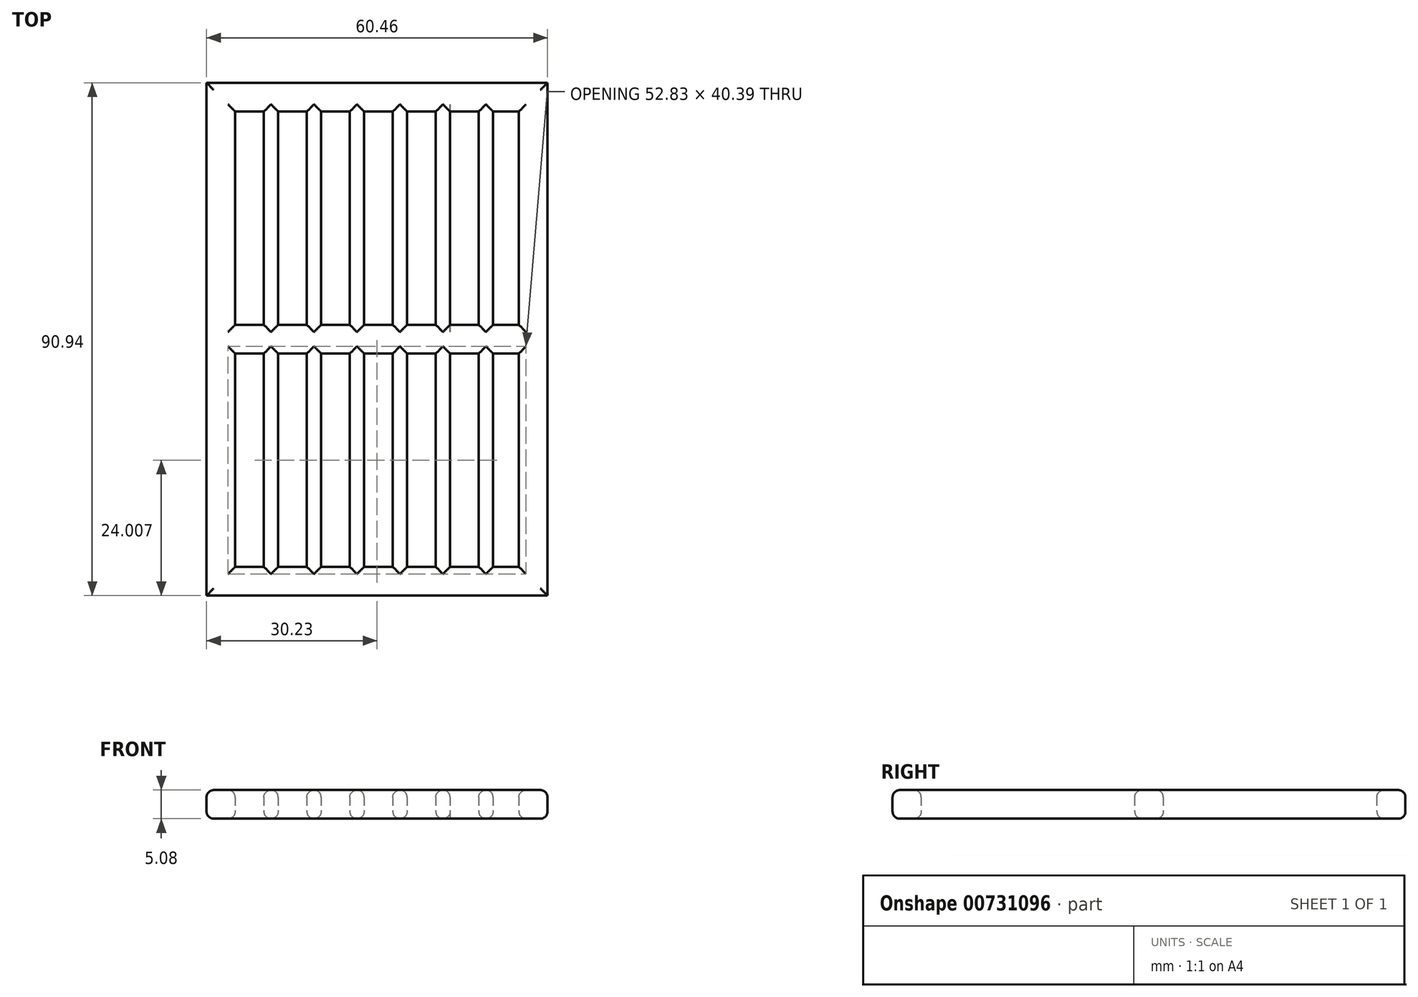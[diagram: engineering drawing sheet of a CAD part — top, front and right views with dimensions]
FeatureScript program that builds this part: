
annotation { "Feature Type Name" : "Feature", "Feature Type Description" : "" }
export const myFeature = defineFeature(function(context is Context, id is Id, definition is map)
    precondition{}
    {
        {
            var Q0;
            Q0=qCreatedBy(makeId("Top.planeOp"),FACE);
            var sketch = newSketch(context, id + "F0", { "sketchPlane" : qUnion([Q0])});
            skLineSegment(sketch, "E0.bottom", {"start": v(-30.23, -45.47) * mm, "end": v(30.23, -45.47) * mm});
            skLineSegment(sketch, "E0.top", {"start": v(-30.23, 45.47) * mm, "end": v(30.23, 45.47) * mm});
            skLineSegment(sketch, "E0.left", {"start": v(-30.23, -45.47) * mm, "end": v(-30.23, 45.47) * mm});
            skLineSegment(sketch, "E0.right", {"start": v(30.23, -45.47) * mm, "end": v(30.23, 45.47) * mm});
            skLineSegment(sketch, "E1.bottom", {"start": v(-25.15, -40.39) * mm, "end": v(25.15, -40.39) * mm});
            skLineSegment(sketch, "E1.top", {"start": v(-25.15, 40.39) * mm, "end": v(25.15, 40.39) * mm});
            skLineSegment(sketch, "E1.left", {"start": v(-25.15, -40.39) * mm, "end": v(-25.15, 40.39) * mm});
            skLineSegment(sketch, "E1.right", {"start": v(25.15, -40.39) * mm, "end": v(25.15, 40.39) * mm});
            skLineSegment(sketch, "E2.bottom", {"start": v(-25.15, 2.54) * mm, "end": v(-2.29, 2.54) * mm});
            skLineSegment(sketch, "E2.top", {"start": v(-25.15, -2.54) * mm, "end": v(25.15, -2.54) * mm});
            skLineSegment(sketch, "E2.left", {"start": v(-25.15, 2.54) * mm, "end": v(-25.15, -2.54) * mm});
            skLineSegment(sketch, "E2.right", {"start": v(25.15, 2.54) * mm, "end": v(25.15, -2.54) * mm});
            skLineSegment(sketch, "E3.bottom", {"start": v(-20.07, 2.54) * mm, "end": v(-17.53, 2.54) * mm});
            skLineSegment(sketch, "E3.top", {"start": v(-20.07, 40.39) * mm, "end": v(-17.53, 40.39) * mm});
            skLineSegment(sketch, "E3.left", {"start": v(-20.07, 2.54) * mm, "end": v(-20.07, 40.39) * mm});
            skLineSegment(sketch, "E3.right", {"start": v(-17.53, 2.54) * mm, "end": v(-17.53, 40.39) * mm});
            skLineSegment(sketch, "E4.bottom", {"start": v(-12.45, 2.54) * mm, "end": v(-9.9, 2.54) * mm});
            skLineSegment(sketch, "E4.top", {"start": v(-12.45, 40.39) * mm, "end": v(-9.9, 40.39) * mm});
            skLineSegment(sketch, "E4.left", {"start": v(-12.45, 2.54) * mm, "end": v(-12.45, 40.39) * mm});
            skLineSegment(sketch, "E4.right", {"start": v(-9.9, 2.54) * mm, "end": v(-9.9, 40.39) * mm});
            skLineSegment(sketch, "E5.bottom", {"start": v(-4.83, 2.54) * mm, "end": v(-2.29, 2.54) * mm});
            skLineSegment(sketch, "E5.top", {"start": v(-4.83, 40.39) * mm, "end": v(-2.29, 40.39) * mm});
            skLineSegment(sketch, "E5.left", {"start": v(-4.83, 2.54) * mm, "end": v(-4.83, 40.39) * mm});
            skLineSegment(sketch, "E5.right", {"start": v(-2.29, 2.54) * mm, "end": v(-2.29, 40.39) * mm});
            skLineSegment(sketch, "E6.bottom", {"start": v(10.41, 2.54) * mm, "end": v(12.95, 2.54) * mm});
            skLineSegment(sketch, "E6.top", {"start": v(10.41, 40.39) * mm, "end": v(12.95, 40.39) * mm});
            skLineSegment(sketch, "E6.left", {"start": v(10.41, 2.54) * mm, "end": v(10.41, 40.39) * mm});
            skLineSegment(sketch, "E6.right", {"start": v(12.95, 2.54) * mm, "end": v(12.95, 40.39) * mm});
            skLineSegment(sketch, "E7.bottom", {"start": v(18.03, 2.54) * mm, "end": v(20.57, 2.54) * mm});
            skLineSegment(sketch, "E7.top", {"start": v(18.03, 40.39) * mm, "end": v(20.57, 40.39) * mm});
            skLineSegment(sketch, "E7.left", {"start": v(18.03, 2.54) * mm, "end": v(18.03, 40.39) * mm});
            skLineSegment(sketch, "E7.right", {"start": v(20.57, 2.54) * mm, "end": v(20.57, 40.39) * mm});
            skLineSegment(sketch, "E8.trimOffspring", {"start": v(10.41, 2.54) * mm, "end": v(25.15, 2.54) * mm});
            skLineSegment(sketch, "E9.bottom", {"start": v(5.33, 2.54) * mm, "end": v(2.8, 2.54) * mm});
            skLineSegment(sketch, "E9.top", {"start": v(5.33, 40.39) * mm, "end": v(2.8, 40.39) * mm});
            skLineSegment(sketch, "E9.left", {"start": v(5.33, 2.54) * mm, "end": v(5.33, 40.39) * mm});
            skLineSegment(sketch, "E9.right", {"start": v(2.8, 2.54) * mm, "end": v(2.8, 40.39) * mm});
            skLineSegment(sketch, "E10.MirrorCS", {"start": v(-20.07, -2.54) * mm, "end": v(-20.07, -40.39) * mm});
            skLineSegment(sketch, "E11.MirrorCS", {"start": v(-17.53, -2.54) * mm, "end": v(-17.53, -40.39) * mm});
            skLineSegment(sketch, "E12.MirrorCS", {"start": v(-12.45, -2.54) * mm, "end": v(-12.45, -40.39) * mm});
            skLineSegment(sketch, "E13.MirrorCS", {"start": v(-9.9, -2.54) * mm, "end": v(-9.9, -40.39) * mm});
            skLineSegment(sketch, "E14.MirrorCS", {"start": v(-4.83, -2.54) * mm, "end": v(-4.83, -40.39) * mm});
            skLineSegment(sketch, "E15.MirrorCS", {"start": v(-2.29, -2.54) * mm, "end": v(-2.29, -40.39) * mm});
            skLineSegment(sketch, "E16.MirrorCS", {"start": v(2.8, -2.54) * mm, "end": v(2.8, -40.39) * mm});
            skLineSegment(sketch, "E17.MirrorCS", {"start": v(5.33, -2.54) * mm, "end": v(5.33, -40.39) * mm});
            skLineSegment(sketch, "E18.MirrorCS", {"start": v(10.41, -2.54) * mm, "end": v(10.41, -40.39) * mm});
            skLineSegment(sketch, "E19.MirrorCS", {"start": v(12.95, -2.54) * mm, "end": v(12.95, -40.39) * mm});
            skLineSegment(sketch, "E20.MirrorCS", {"start": v(18.03, -2.54) * mm, "end": v(18.03, -40.39) * mm});
            skLineSegment(sketch, "E21.MirrorCS", {"start": v(20.57, -2.54) * mm, "end": v(20.57, -40.39) * mm});
            skLineSegment(sketch, "E22", {"start": v(-2.29, 2.54) * mm, "end": v(2.8, 2.54) * mm});
            skLineSegment(sketch, "E23", {"start": v(5.33, 2.54) * mm, "end": v(10.41, 2.54) * mm});
            skSolve(sketch);
        }
        {
            var Q0;
            Q0=makeQuery(id+"F0.imprint","IMPRINT",FACE,{"disambiguationData":[TD([[makeQuery(id+"F0.imprint","IMPRINT",EDGE,{"derivedFrom":sQuery(id+"F0.wireOp",EDGE,"E0.bottom")}),1.0]])]});
            var Q1;
            {var subQ25=sQuery(id+"F0.wireOp",EDGE,"E6.bottom");Q1=makeQuery(id+"F0.imprint","IMPRINT",FACE,{"disambiguationData":[TD([[makeQuery(id+"F0.imprint","IMPRINT",EDGE,{"derivedFrom":subQ25}),-1.0]])]});}
            var Q2;
            {var subQ0=sQuery(id+"F0.wireOp",EDGE,"E10.MirrorCS");Q2=makeQuery(id+"F0.imprint","IMPRINT",FACE,{"disambiguationData":[TD([[makeQuery(id+"F0.imprint","IMPRINT",EDGE,{"derivedFrom":subQ0}),1.0]])]});}
            var Q3;
            {var subQ2=sQuery(id+"F0.wireOp",EDGE,"E12.MirrorCS");Q3=makeQuery(id+"F0.imprint","IMPRINT",FACE,{"disambiguationData":[TD([[makeQuery(id+"F0.imprint","IMPRINT",EDGE,{"derivedFrom":subQ2}),1.0]])]});}
            var Q4;
            {var subQ0=sQuery(id+"F0.wireOp",EDGE,"E14.MirrorCS");Q4=makeQuery(id+"F0.imprint","IMPRINT",FACE,{"disambiguationData":[TD([[makeQuery(id+"F0.imprint","IMPRINT",EDGE,{"derivedFrom":subQ0}),1.0]])]});}
            var Q5;
            {var subQ0=sQuery(id+"F0.wireOp",EDGE,"E16.MirrorCS");Q5=makeQuery(id+"F0.imprint","IMPRINT",FACE,{"disambiguationData":[TD([[makeQuery(id+"F0.imprint","IMPRINT",EDGE,{"derivedFrom":subQ0}),1.0]])]});}
            var Q6;
            {var subQ0=sQuery(id+"F0.wireOp",EDGE,"E18.MirrorCS");Q6=makeQuery(id+"F0.imprint","IMPRINT",FACE,{"disambiguationData":[TD([[makeQuery(id+"F0.imprint","IMPRINT",EDGE,{"derivedFrom":subQ0}),1.0]])]});}
            var Q7;
            {var subQ0=sQuery(id+"F0.wireOp",EDGE,"E20.MirrorCS");Q7=makeQuery(id+"F0.imprint","IMPRINT",FACE,{"disambiguationData":[TD([[makeQuery(id+"F0.imprint","IMPRINT",EDGE,{"derivedFrom":subQ0}),1.0]])]});}
            var Q8;
            Q8=makeQuery(id+"F0.imprint","IMPRINT",FACE,{"disambiguationData":[TD([[makeQuery(id+"F0.imprint","IMPRINT",EDGE,{"derivedFrom":sQuery(id+"F0.wireOp",EDGE,"E7.bottom")}),1.0]])]});
            var Q9;
            Q9=makeQuery(id+"F0.imprint","IMPRINT",FACE,{"disambiguationData":[TD([[makeQuery(id+"F0.imprint","IMPRINT",EDGE,{"derivedFrom":sQuery(id+"F0.wireOp",EDGE,"E6.bottom")}),1.0]])]});
            var Q10;
            Q10=makeQuery(id+"F0.imprint","IMPRINT",FACE,{"disambiguationData":[TD([[makeQuery(id+"F0.imprint","IMPRINT",EDGE,{"derivedFrom":sQuery(id+"F0.wireOp",EDGE,"E9.bottom")}),-1.0]])]});
            var Q11;
            {var subQ0=sQuery(id+"F0.wireOp",EDGE,"E5.left");Q11=makeQuery(id+"F0.imprint","IMPRINT",FACE,{"disambiguationData":[TD([[makeQuery(id+"F0.imprint","IMPRINT",EDGE,{"derivedFrom":subQ0}),-1.0]])]});}
            var Q12;
            {var subQ0=sQuery(id+"F0.wireOp",EDGE,"E4.left");Q12=makeQuery(id+"F0.imprint","IMPRINT",FACE,{"disambiguationData":[TD([[makeQuery(id+"F0.imprint","IMPRINT",EDGE,{"derivedFrom":subQ0}),-1.0]])]});}
            var Q13;
            {var subQ0=sQuery(id+"F0.wireOp",EDGE,"E3.left");Q13=makeQuery(id+"F0.imprint","IMPRINT",FACE,{"disambiguationData":[TD([[makeQuery(id+"F0.imprint","IMPRINT",EDGE,{"derivedFrom":subQ0}),-1.0]])]});}
            extrude(context, id + "F1", {"entities" : qUnion([Q0, Q1, Q2, Q3, Q4, Q5, Q6, Q7, Q8, Q9, Q10, Q11, Q12, Q13]), "depth" : 5.08 * mm, "offsetDistance" : 25.4 * mm});
        }
        {
            var Q0;
            Q0=makeQuery(id+"F1.opExtrude","CAP_EDGE",EDGE,{"disambiguationData":[OSD([sQuery(id+"F0.wireOp",EDGE,"E3.left")])],"isStart":false});
            var Q1;
            {var subQ0=sQuery(id+"F0.wireOp",EDGE,"E1.top");Q1=makeQuery(id+"F1.opExtrude","CAP_EDGE",EDGE,{"disambiguationData":[OSD([subQ0]),TDD([makeQuery(id+"F0.imprint","IMPRINT",EDGE,{"disambiguationData":[TD([[makeQuery(id+"F0.imprint","INTERSECT",VERTEX,{"derivedFrom":[subQ0,sQuery(id+"F0.wireOp",EDGE,"E3.left")]}),1.0]])],"derivedFrom":subQ0})])],"isStart":false});}
            var Q2;
            {var subQ0=sQuery(id+"F0.wireOp",EDGE,"E1.left");Q2=makeQuery(id+"F1.opExtrude","CAP_EDGE",EDGE,{"disambiguationData":[OSD([subQ0]),TDD([makeQuery(id+"F0.imprint","IMPRINT",EDGE,{"disambiguationData":[TD([[makeQuery(id+"F0.imprint","INTERSECT",VERTEX,{"derivedFrom":[subQ0,sQuery(id+"F0.wireOp",EDGE,"E2.bottom")]}),-1.0]])],"derivedFrom":subQ0})])],"isStart":false});}
            var Q3;
            {var subQ0=sQuery(id+"F0.wireOp",EDGE,"E2.bottom");Q3=makeQuery(id+"F1.opExtrude","CAP_EDGE",EDGE,{"disambiguationData":[OSD([subQ0]),TDD([makeQuery(id+"F0.imprint","IMPRINT",EDGE,{"disambiguationData":[TD([[makeQuery(id+"F0.imprint","INTERSECT",VERTEX,{"derivedFrom":[sQuery(id+"F0.wireOp",EDGE,"E1.left"),subQ0]}),-1.0]])],"derivedFrom":subQ0})])],"isStart":false});}
            var Q4;
            Q4=makeQuery(id+"F1.opExtrude","CAP_EDGE",EDGE,{"disambiguationData":[OSD([sQuery(id+"F0.wireOp",EDGE,"E3.right")])],"isStart":false});
            var Q5;
            Q5=makeQuery(id+"F1.opExtrude","CAP_EDGE",EDGE,{"disambiguationData":[OSD([sQuery(id+"F0.wireOp",EDGE,"E4.left")])],"isStart":false});
            var Q6;
            {var subQ0=sQuery(id+"F0.wireOp",EDGE,"E1.top");Q6=makeQuery(id+"F1.opExtrude","CAP_EDGE",EDGE,{"disambiguationData":[OSD([subQ0]),TDD([makeQuery(id+"F0.imprint","IMPRINT",EDGE,{"disambiguationData":[TD([[makeQuery(id+"F0.imprint","INTERSECT",VERTEX,{"derivedFrom":[subQ0,sQuery(id+"F0.wireOp",EDGE,"E3.right")]}),-1.0]])],"derivedFrom":subQ0})])],"isStart":false});}
            var Q7;
            {var subQ0=sQuery(id+"F0.wireOp",EDGE,"E2.bottom");Q7=makeQuery(id+"F1.opExtrude","CAP_EDGE",EDGE,{"disambiguationData":[OSD([subQ0]),TDD([makeQuery(id+"F0.imprint","IMPRINT",EDGE,{"disambiguationData":[TD([[makeQuery(id+"F0.imprint","INTERSECT",VERTEX,{"derivedFrom":[subQ0,sQuery(id+"F0.wireOp",EDGE,"E3.right")]}),-1.0]])],"derivedFrom":subQ0})])],"isStart":false});}
            var Q8;
            {var subQ0=sQuery(id+"F0.wireOp",EDGE,"E2.bottom");Q8=makeQuery(id+"F1.opExtrude","CAP_EDGE",EDGE,{"disambiguationData":[OSD([subQ0]),TDD([makeQuery(id+"F0.imprint","IMPRINT",EDGE,{"disambiguationData":[TD([[makeQuery(id+"F0.imprint","INTERSECT",VERTEX,{"derivedFrom":[subQ0,sQuery(id+"F0.wireOp",EDGE,"E4.right")]}),-1.0]])],"derivedFrom":subQ0})])],"isStart":false});}
            var Q9;
            Q9=makeQuery(id+"F1.opExtrude","CAP_EDGE",EDGE,{"disambiguationData":[OSD([sQuery(id+"F0.wireOp",EDGE,"E5.left")])],"isStart":false});
            var Q10;
            Q10=makeQuery(id+"F1.opExtrude","CAP_EDGE",EDGE,{"disambiguationData":[OSD([sQuery(id+"F0.wireOp",EDGE,"E4.right")])],"isStart":false});
            var Q11;
            {var subQ0=sQuery(id+"F0.wireOp",EDGE,"E1.top");Q11=makeQuery(id+"F1.opExtrude","CAP_EDGE",EDGE,{"disambiguationData":[OSD([subQ0]),TDD([makeQuery(id+"F0.imprint","IMPRINT",EDGE,{"disambiguationData":[TD([[makeQuery(id+"F0.imprint","INTERSECT",VERTEX,{"derivedFrom":[subQ0,sQuery(id+"F0.wireOp",EDGE,"E4.right")]}),-1.0]])],"derivedFrom":subQ0})])],"isStart":false});}
            var Q12;
            Q12=makeQuery(id+"F1.opExtrude","CAP_EDGE",EDGE,{"disambiguationData":[OSD([sQuery(id+"F0.wireOp",EDGE,"E5.right")])],"isStart":false});
            var Q13;
            Q13=makeQuery(id+"F1.opExtrude","CAP_EDGE",EDGE,{"disambiguationData":[OSD([sQuery(id+"F0.wireOp",EDGE,"E9.right")])],"isStart":false});
            var Q14;
            {var subQ0=sQuery(id+"F0.wireOp",EDGE,"E1.top");Q14=makeQuery(id+"F1.opExtrude","CAP_EDGE",EDGE,{"disambiguationData":[OSD([subQ0]),TDD([makeQuery(id+"F0.imprint","IMPRINT",EDGE,{"disambiguationData":[TD([[makeQuery(id+"F0.imprint","INTERSECT",VERTEX,{"derivedFrom":[subQ0,sQuery(id+"F0.wireOp",EDGE,"E5.right")]}),-1.0]])],"derivedFrom":subQ0})])],"isStart":false});}
            var Q15;
            Q15=makeQuery(id+"F1.opExtrude","CAP_EDGE",EDGE,{"disambiguationData":[OSD([sQuery(id+"F0.wireOp",EDGE,"E22")])],"isStart":false});
            var Q16;
            Q16=makeQuery(id+"F1.opExtrude","CAP_EDGE",EDGE,{"disambiguationData":[OSD([sQuery(id+"F0.wireOp",EDGE,"E9.left")])],"isStart":false});
            var Q17;
            Q17=makeQuery(id+"F1.opExtrude","CAP_EDGE",EDGE,{"disambiguationData":[OSD([sQuery(id+"F0.wireOp",EDGE,"E23")])],"isStart":false});
            var Q18;
            Q18=makeQuery(id+"F1.opExtrude","CAP_EDGE",EDGE,{"disambiguationData":[OSD([sQuery(id+"F0.wireOp",EDGE,"E6.left")])],"isStart":false});
            var Q19;
            {var subQ0=sQuery(id+"F0.wireOp",EDGE,"E1.top");Q19=makeQuery(id+"F1.opExtrude","CAP_EDGE",EDGE,{"disambiguationData":[OSD([subQ0]),TDD([makeQuery(id+"F0.imprint","IMPRINT",EDGE,{"disambiguationData":[TD([[makeQuery(id+"F0.imprint","INTERSECT",VERTEX,{"derivedFrom":[subQ0,sQuery(id+"F0.wireOp",EDGE,"E9.left")]}),-1.0]])],"derivedFrom":subQ0})])],"isStart":false});}
            var Q20;
            Q20=makeQuery(id+"F1.opExtrude","CAP_EDGE",EDGE,{"disambiguationData":[OSD([sQuery(id+"F0.wireOp",EDGE,"E6.right")])],"isStart":false});
            var Q21;
            Q21=makeQuery(id+"F1.opExtrude","CAP_EDGE",EDGE,{"disambiguationData":[OSD([sQuery(id+"F0.wireOp",EDGE,"E7.left")])],"isStart":false});
            var Q22;
            {var subQ0=sQuery(id+"F0.wireOp",EDGE,"E8.trimOffspring");Q22=makeQuery(id+"F1.opExtrude","CAP_EDGE",EDGE,{"disambiguationData":[OSD([subQ0]),TDD([makeQuery(id+"F0.imprint","IMPRINT",EDGE,{"disambiguationData":[TD([[makeQuery(id+"F0.imprint","INTERSECT",VERTEX,{"derivedFrom":[sQuery(id+"F0.wireOp",EDGE,"E6.bottom"),sQuery(id+"F0.wireOp",EDGE,"E6.right"),subQ0]}),-1.0]])],"derivedFrom":subQ0})])],"isStart":false});}
            var Q23;
            {var subQ0=sQuery(id+"F0.wireOp",EDGE,"E1.top");Q23=makeQuery(id+"F1.opExtrude","CAP_EDGE",EDGE,{"disambiguationData":[OSD([subQ0]),TDD([makeQuery(id+"F0.imprint","IMPRINT",EDGE,{"disambiguationData":[TD([[makeQuery(id+"F0.imprint","INTERSECT",VERTEX,{"derivedFrom":[subQ0,sQuery(id+"F0.wireOp",EDGE,"E6.right")]}),-1.0]])],"derivedFrom":subQ0})])],"isStart":false});}
            var Q24;
            {var subQ0=sQuery(id+"F0.wireOp",EDGE,"E1.top");Q24=makeQuery(id+"F1.opExtrude","CAP_EDGE",EDGE,{"disambiguationData":[OSD([subQ0]),TDD([makeQuery(id+"F0.imprint","IMPRINT",EDGE,{"disambiguationData":[TD([[makeQuery(id+"F0.imprint","INTERSECT",VERTEX,{"derivedFrom":[subQ0,sQuery(id+"F0.wireOp",EDGE,"E7.right")]}),-1.0]])],"derivedFrom":subQ0})])],"isStart":false});}
            var Q25;
            {var subQ0=sQuery(id+"F0.wireOp",EDGE,"E1.right");Q25=makeQuery(id+"F1.opExtrude","CAP_EDGE",EDGE,{"disambiguationData":[OSD([subQ0]),TDD([makeQuery(id+"F0.imprint","IMPRINT",EDGE,{"disambiguationData":[TD([[makeQuery(id+"F0.imprint","INTERSECT",VERTEX,{"derivedFrom":[subQ0,sQuery(id+"F0.wireOp",EDGE,"E8.trimOffspring")]}),-1.0]])],"derivedFrom":subQ0})])],"isStart":false});}
            var Q26;
            Q26=makeQuery(id+"F1.opExtrude","CAP_EDGE",EDGE,{"disambiguationData":[OSD([sQuery(id+"F0.wireOp",EDGE,"E7.right")])],"isStart":false});
            var Q27;
            {var subQ0=sQuery(id+"F0.wireOp",EDGE,"E8.trimOffspring");Q27=makeQuery(id+"F1.opExtrude","CAP_EDGE",EDGE,{"disambiguationData":[OSD([subQ0]),TDD([makeQuery(id+"F0.imprint","IMPRINT",EDGE,{"disambiguationData":[TD([[makeQuery(id+"F0.imprint","INTERSECT",VERTEX,{"derivedFrom":[sQuery(id+"F0.wireOp",EDGE,"E1.right"),subQ0]}),1.0]])],"derivedFrom":subQ0})])],"isStart":false});}
            var Q28;
            {var subQ0=sQuery(id+"F0.wireOp",EDGE,"E1.right");Q28=makeQuery(id+"F1.opExtrude","CAP_EDGE",EDGE,{"disambiguationData":[OSD([subQ0]),TDD([makeQuery(id+"F0.imprint","IMPRINT",EDGE,{"disambiguationData":[TD([[makeQuery(id+"F0.imprint","INTERSECT",VERTEX,{"derivedFrom":[sQuery(id+"F0.wireOp",EDGE,"E1.bottom"),subQ0]}),-1.0]])],"derivedFrom":subQ0})])],"isStart":false});}
            var Q29;
            Q29=makeQuery(id+"F1.opExtrude","CAP_EDGE",EDGE,{"disambiguationData":[OSD([sQuery(id+"F0.wireOp",EDGE,"E21.MirrorCS")])],"isStart":false});
            var Q30;
            {var subQ0=sQuery(id+"F0.wireOp",EDGE,"E2.top");Q30=makeQuery(id+"F1.opExtrude","CAP_EDGE",EDGE,{"disambiguationData":[OSD([subQ0]),TDD([makeQuery(id+"F0.imprint","IMPRINT",EDGE,{"disambiguationData":[TD([[makeQuery(id+"F0.imprint","INTERSECT",VERTEX,{"derivedFrom":[subQ0,sQuery(id+"F0.wireOp",EDGE,"E21.MirrorCS")]}),-1.0]])],"derivedFrom":subQ0})])],"isStart":false});}
            var Q31;
            {var subQ0=sQuery(id+"F0.wireOp",EDGE,"E1.bottom");Q31=makeQuery(id+"F1.opExtrude","CAP_EDGE",EDGE,{"disambiguationData":[OSD([subQ0]),TDD([makeQuery(id+"F0.imprint","IMPRINT",EDGE,{"disambiguationData":[TD([[makeQuery(id+"F0.imprint","INTERSECT",VERTEX,{"derivedFrom":[subQ0,sQuery(id+"F0.wireOp",EDGE,"E1.right")]}),1.0]])],"derivedFrom":subQ0})])],"isStart":false});}
            var Q32;
            {var subQ0=sQuery(id+"F0.wireOp",EDGE,"E1.bottom");Q32=makeQuery(id+"F1.opExtrude","CAP_EDGE",EDGE,{"disambiguationData":[OSD([subQ0]),TDD([makeQuery(id+"F0.imprint","IMPRINT",EDGE,{"disambiguationData":[TD([[makeQuery(id+"F0.imprint","INTERSECT",VERTEX,{"derivedFrom":[subQ0,sQuery(id+"F0.wireOp",EDGE,"E19.MirrorCS")]}),-1.0]])],"derivedFrom":subQ0})])],"isStart":false});}
            var Q33;
            Q33=makeQuery(id+"F1.opExtrude","CAP_EDGE",EDGE,{"disambiguationData":[OSD([sQuery(id+"F0.wireOp",EDGE,"E20.MirrorCS")])],"isStart":false});
            var Q34;
            Q34=makeQuery(id+"F1.opExtrude","CAP_EDGE",EDGE,{"disambiguationData":[OSD([sQuery(id+"F0.wireOp",EDGE,"E19.MirrorCS")])],"isStart":false});
            var Q35;
            {var subQ0=sQuery(id+"F0.wireOp",EDGE,"E2.top");Q35=makeQuery(id+"F1.opExtrude","CAP_EDGE",EDGE,{"disambiguationData":[OSD([subQ0]),TDD([makeQuery(id+"F0.imprint","IMPRINT",EDGE,{"disambiguationData":[TD([[makeQuery(id+"F0.imprint","INTERSECT",VERTEX,{"derivedFrom":[subQ0,sQuery(id+"F0.wireOp",EDGE,"E19.MirrorCS")]}),-1.0]])],"derivedFrom":subQ0})])],"isStart":false});}
            var Q36;
            {var subQ0=sQuery(id+"F0.wireOp",EDGE,"E2.top");Q36=makeQuery(id+"F1.opExtrude","CAP_EDGE",EDGE,{"disambiguationData":[OSD([subQ0]),TDD([makeQuery(id+"F0.imprint","IMPRINT",EDGE,{"disambiguationData":[TD([[makeQuery(id+"F0.imprint","INTERSECT",VERTEX,{"derivedFrom":[subQ0,sQuery(id+"F0.wireOp",EDGE,"E17.MirrorCS")]}),-1.0]])],"derivedFrom":subQ0})])],"isStart":false});}
            var Q37;
            Q37=makeQuery(id+"F1.opExtrude","CAP_EDGE",EDGE,{"disambiguationData":[OSD([sQuery(id+"F0.wireOp",EDGE,"E17.MirrorCS")])],"isStart":false});
            var Q38;
            Q38=makeQuery(id+"F1.opExtrude","CAP_EDGE",EDGE,{"disambiguationData":[OSD([sQuery(id+"F0.wireOp",EDGE,"E18.MirrorCS")])],"isStart":false});
            var Q39;
            {var subQ0=sQuery(id+"F0.wireOp",EDGE,"E1.bottom");Q39=makeQuery(id+"F1.opExtrude","CAP_EDGE",EDGE,{"disambiguationData":[OSD([subQ0]),TDD([makeQuery(id+"F0.imprint","IMPRINT",EDGE,{"disambiguationData":[TD([[makeQuery(id+"F0.imprint","INTERSECT",VERTEX,{"derivedFrom":[subQ0,sQuery(id+"F0.wireOp",EDGE,"E17.MirrorCS")]}),-1.0]])],"derivedFrom":subQ0})])],"isStart":false});}
            var Q40;
            Q40=makeQuery(id+"F1.opExtrude","CAP_EDGE",EDGE,{"disambiguationData":[OSD([sQuery(id+"F0.wireOp",EDGE,"E15.MirrorCS")])],"isStart":false});
            var Q41;
            Q41=makeQuery(id+"F1.opExtrude","CAP_EDGE",EDGE,{"disambiguationData":[OSD([sQuery(id+"F0.wireOp",EDGE,"E16.MirrorCS")])],"isStart":false});
            var Q42;
            {var subQ0=sQuery(id+"F0.wireOp",EDGE,"E1.bottom");Q42=makeQuery(id+"F1.opExtrude","CAP_EDGE",EDGE,{"disambiguationData":[OSD([subQ0]),TDD([makeQuery(id+"F0.imprint","IMPRINT",EDGE,{"disambiguationData":[TD([[makeQuery(id+"F0.imprint","INTERSECT",VERTEX,{"derivedFrom":[subQ0,sQuery(id+"F0.wireOp",EDGE,"E15.MirrorCS")]}),-1.0]])],"derivedFrom":subQ0})])],"isStart":false});}
            var Q43;
            {var subQ0=sQuery(id+"F0.wireOp",EDGE,"E2.top");Q43=makeQuery(id+"F1.opExtrude","CAP_EDGE",EDGE,{"disambiguationData":[OSD([subQ0]),TDD([makeQuery(id+"F0.imprint","IMPRINT",EDGE,{"disambiguationData":[TD([[makeQuery(id+"F0.imprint","INTERSECT",VERTEX,{"derivedFrom":[subQ0,sQuery(id+"F0.wireOp",EDGE,"E15.MirrorCS")]}),-1.0]])],"derivedFrom":subQ0})])],"isStart":false});}
            var Q44;
            Q44=makeQuery(id+"F1.opExtrude","CAP_EDGE",EDGE,{"disambiguationData":[OSD([sQuery(id+"F0.wireOp",EDGE,"E14.MirrorCS")])],"isStart":false});
            var Q45;
            Q45=makeQuery(id+"F1.opExtrude","CAP_EDGE",EDGE,{"disambiguationData":[OSD([sQuery(id+"F0.wireOp",EDGE,"E13.MirrorCS")])],"isStart":false});
            var Q46;
            {var subQ0=sQuery(id+"F0.wireOp",EDGE,"E2.top");Q46=makeQuery(id+"F1.opExtrude","CAP_EDGE",EDGE,{"disambiguationData":[OSD([subQ0]),TDD([makeQuery(id+"F0.imprint","IMPRINT",EDGE,{"disambiguationData":[TD([[makeQuery(id+"F0.imprint","INTERSECT",VERTEX,{"derivedFrom":[subQ0,sQuery(id+"F0.wireOp",EDGE,"E13.MirrorCS")]}),-1.0]])],"derivedFrom":subQ0})])],"isStart":false});}
            var Q47;
            {var subQ0=sQuery(id+"F0.wireOp",EDGE,"E1.bottom");Q47=makeQuery(id+"F1.opExtrude","CAP_EDGE",EDGE,{"disambiguationData":[OSD([subQ0]),TDD([makeQuery(id+"F0.imprint","IMPRINT",EDGE,{"disambiguationData":[TD([[makeQuery(id+"F0.imprint","INTERSECT",VERTEX,{"derivedFrom":[subQ0,sQuery(id+"F0.wireOp",EDGE,"E13.MirrorCS")]}),-1.0]])],"derivedFrom":subQ0})])],"isStart":false});}
            var Q48;
            {var subQ0=sQuery(id+"F0.wireOp",EDGE,"E1.bottom");Q48=makeQuery(id+"F1.opExtrude","CAP_EDGE",EDGE,{"disambiguationData":[OSD([subQ0]),TDD([makeQuery(id+"F0.imprint","IMPRINT",EDGE,{"disambiguationData":[TD([[makeQuery(id+"F0.imprint","INTERSECT",VERTEX,{"derivedFrom":[subQ0,sQuery(id+"F0.wireOp",EDGE,"E11.MirrorCS")]}),-1.0]])],"derivedFrom":subQ0})])],"isStart":false});}
            var Q49;
            {var subQ0=sQuery(id+"F0.wireOp",EDGE,"E2.top");Q49=makeQuery(id+"F1.opExtrude","CAP_EDGE",EDGE,{"disambiguationData":[OSD([subQ0]),TDD([makeQuery(id+"F0.imprint","IMPRINT",EDGE,{"disambiguationData":[TD([[makeQuery(id+"F0.imprint","INTERSECT",VERTEX,{"derivedFrom":[subQ0,sQuery(id+"F0.wireOp",EDGE,"E11.MirrorCS")]}),-1.0]])],"derivedFrom":subQ0})])],"isStart":false});}
            var Q50;
            Q50=makeQuery(id+"F1.opExtrude","CAP_EDGE",EDGE,{"disambiguationData":[OSD([sQuery(id+"F0.wireOp",EDGE,"E11.MirrorCS")])],"isStart":false});
            var Q51;
            Q51=makeQuery(id+"F1.opExtrude","CAP_EDGE",EDGE,{"disambiguationData":[OSD([sQuery(id+"F0.wireOp",EDGE,"E12.MirrorCS")])],"isStart":false});
            var Q52;
            Q52=makeQuery(id+"F1.opExtrude","CAP_FACE",FACE,{"disambiguationData":[OSD([sQuery(id+"F0.wireOp",EDGE,"E0.bottom"),sQuery(id+"F0.wireOp",EDGE,"E0.top"),sQuery(id+"F0.wireOp",EDGE,"E0.left"),sQuery(id+"F0.wireOp",EDGE,"E0.right"),sQuery(id+"F0.wireOp",EDGE,"E1.bottom"),sQuery(id+"F0.wireOp",EDGE,"E1.top"),sQuery(id+"F0.wireOp",EDGE,"E1.left"),sQuery(id+"F0.wireOp",EDGE,"E1.right"),sQuery(id+"F0.wireOp",EDGE,"E2.bottom"),sQuery(id+"F0.wireOp",EDGE,"E2.top"),sQuery(id+"F0.wireOp",EDGE,"E3.left"),sQuery(id+"F0.wireOp",EDGE,"E3.right"),sQuery(id+"F0.wireOp",EDGE,"E4.left"),sQuery(id+"F0.wireOp",EDGE,"E4.right"),sQuery(id+"F0.wireOp",EDGE,"E5.left"),sQuery(id+"F0.wireOp",EDGE,"E5.right"),sQuery(id+"F0.wireOp",EDGE,"E6.left"),sQuery(id+"F0.wireOp",EDGE,"E6.right"),sQuery(id+"F0.wireOp",EDGE,"E7.left"),sQuery(id+"F0.wireOp",EDGE,"E7.right"),sQuery(id+"F0.wireOp",EDGE,"E8.trimOffspring"),sQuery(id+"F0.wireOp",EDGE,"E9.left"),sQuery(id+"F0.wireOp",EDGE,"E9.right"),sQuery(id+"F0.wireOp",EDGE,"E10.MirrorCS"),sQuery(id+"F0.wireOp",EDGE,"E11.MirrorCS"),sQuery(id+"F0.wireOp",EDGE,"E12.MirrorCS"),sQuery(id+"F0.wireOp",EDGE,"E13.MirrorCS"),sQuery(id+"F0.wireOp",EDGE,"E14.MirrorCS"),sQuery(id+"F0.wireOp",EDGE,"E15.MirrorCS"),sQuery(id+"F0.wireOp",EDGE,"E16.MirrorCS"),sQuery(id+"F0.wireOp",EDGE,"E17.MirrorCS"),sQuery(id+"F0.wireOp",EDGE,"E18.MirrorCS"),sQuery(id+"F0.wireOp",EDGE,"E19.MirrorCS"),sQuery(id+"F0.wireOp",EDGE,"E20.MirrorCS"),sQuery(id+"F0.wireOp",EDGE,"E21.MirrorCS"),sQuery(id+"F0.wireOp",EDGE,"E22"),sQuery(id+"F0.wireOp",EDGE,"E23")])],"isStart":false});
            var Q53;
            {var subQ0=sQuery(id+"F0.wireOp",EDGE,"E2.top");Q53=makeQuery(id+"F1.opExtrude","CAP_EDGE",EDGE,{"disambiguationData":[OSD([subQ0]),TDD([makeQuery(id+"F0.imprint","IMPRINT",EDGE,{"disambiguationData":[TD([[makeQuery(id+"F0.imprint","INTERSECT",VERTEX,{"derivedFrom":[sQuery(id+"F0.wireOp",EDGE,"E1.left"),subQ0]}),-1.0]])],"derivedFrom":subQ0})])],"isStart":false});}
            fillet(context, id + "F2", {"entities" : qUnion([Q0, Q1, Q2, Q3, Q4, Q5, Q6, Q7, Q8, Q9, Q10, Q11, Q12, Q13, Q14, Q15, Q16, Q17, Q18, Q19, Q20, Q21, Q22, Q23, Q24, Q25, Q26, Q27, Q28, Q29, Q30, Q31, Q32, Q33, Q34, Q35, Q36, Q37, Q38, Q39, Q40, Q41, Q42, Q43, Q44, Q45, Q46, Q47, Q48, Q49, Q50, Q51, Q52, Q53]), "radius" : 1.27 * mm, "tangentPropagation" : true, "allowEdgeOverflow" : false});
        }
        {
            var Q0;
            {var subQ0=sQuery(id+"F0.wireOp",EDGE,"E1.right");Q0=makeQuery(id+"F1.opExtrude","CAP_EDGE",EDGE,{"disambiguationData":[OSD([subQ0]),TDD([makeQuery(id+"F0.imprint","IMPRINT",EDGE,{"disambiguationData":[TD([[makeQuery(id+"F0.imprint","INTERSECT",VERTEX,{"derivedFrom":[subQ0,sQuery(id+"F0.wireOp",EDGE,"E8.trimOffspring")]}),-1.0]])],"derivedFrom":subQ0})])],"isStart":true});}
            var Q1;
            Q1=makeQuery(id+"F1.opExtrude","CAP_EDGE",EDGE,{"disambiguationData":[OSD([sQuery(id+"F0.wireOp",EDGE,"E7.right")])],"isStart":true});
            var Q2;
            Q2=makeQuery(id+"F1.opExtrude","CAP_EDGE",EDGE,{"disambiguationData":[OSD([sQuery(id+"F0.wireOp",EDGE,"E7.left")])],"isStart":true});
            var Q3;
            Q3=makeQuery(id+"F1.opExtrude","CAP_EDGE",EDGE,{"disambiguationData":[OSD([sQuery(id+"F0.wireOp",EDGE,"E6.left")])],"isStart":true});
            var Q4;
            Q4=makeQuery(id+"F1.opExtrude","CAP_EDGE",EDGE,{"disambiguationData":[OSD([sQuery(id+"F0.wireOp",EDGE,"E9.left")])],"isStart":true});
            var Q5;
            Q5=makeQuery(id+"F1.opExtrude","CAP_EDGE",EDGE,{"disambiguationData":[OSD([sQuery(id+"F0.wireOp",EDGE,"E9.right")])],"isStart":true});
            var Q6;
            Q6=makeQuery(id+"F1.opExtrude","CAP_EDGE",EDGE,{"disambiguationData":[OSD([sQuery(id+"F0.wireOp",EDGE,"E5.right")])],"isStart":true});
            var Q7;
            Q7=makeQuery(id+"F1.opExtrude","CAP_EDGE",EDGE,{"disambiguationData":[OSD([sQuery(id+"F0.wireOp",EDGE,"E5.left")])],"isStart":true});
            var Q8;
            Q8=makeQuery(id+"F1.opExtrude","CAP_EDGE",EDGE,{"disambiguationData":[OSD([sQuery(id+"F0.wireOp",EDGE,"E4.right")])],"isStart":true});
            var Q9;
            Q9=makeQuery(id+"F1.opExtrude","CAP_EDGE",EDGE,{"disambiguationData":[OSD([sQuery(id+"F0.wireOp",EDGE,"E4.left")])],"isStart":true});
            var Q10;
            Q10=makeQuery(id+"F1.opExtrude","CAP_EDGE",EDGE,{"disambiguationData":[OSD([sQuery(id+"F0.wireOp",EDGE,"E3.right")])],"isStart":true});
            var Q11;
            Q11=makeQuery(id+"F1.opExtrude","CAP_EDGE",EDGE,{"disambiguationData":[OSD([sQuery(id+"F0.wireOp",EDGE,"E3.left")])],"isStart":true});
            var Q12;
            {var subQ0=sQuery(id+"F0.wireOp",EDGE,"E1.left");Q12=makeQuery(id+"F1.opExtrude","CAP_EDGE",EDGE,{"disambiguationData":[OSD([subQ0]),TDD([makeQuery(id+"F0.imprint","IMPRINT",EDGE,{"disambiguationData":[TD([[makeQuery(id+"F0.imprint","INTERSECT",VERTEX,{"derivedFrom":[subQ0,sQuery(id+"F0.wireOp",EDGE,"E2.bottom")]}),-1.0]])],"derivedFrom":subQ0})])],"isStart":true});}
            var Q13;
            {var subQ0=sQuery(id+"F0.wireOp",EDGE,"E1.top");Q13=makeQuery(id+"F1.opExtrude","CAP_EDGE",EDGE,{"disambiguationData":[OSD([subQ0]),TDD([makeQuery(id+"F0.imprint","IMPRINT",EDGE,{"disambiguationData":[TD([[makeQuery(id+"F0.imprint","INTERSECT",VERTEX,{"derivedFrom":[subQ0,sQuery(id+"F0.wireOp",EDGE,"E3.right")]}),-1.0]])],"derivedFrom":subQ0})])],"isStart":true});}
            var Q14;
            {var subQ0=sQuery(id+"F0.wireOp",EDGE,"E1.top");Q14=makeQuery(id+"F1.opExtrude","CAP_EDGE",EDGE,{"disambiguationData":[OSD([subQ0]),TDD([makeQuery(id+"F0.imprint","IMPRINT",EDGE,{"disambiguationData":[TD([[makeQuery(id+"F0.imprint","INTERSECT",VERTEX,{"derivedFrom":[subQ0,sQuery(id+"F0.wireOp",EDGE,"E4.right")]}),-1.0]])],"derivedFrom":subQ0})])],"isStart":true});}
            var Q15;
            {var subQ0=sQuery(id+"F0.wireOp",EDGE,"E1.top");Q15=makeQuery(id+"F1.opExtrude","CAP_EDGE",EDGE,{"disambiguationData":[OSD([subQ0]),TDD([makeQuery(id+"F0.imprint","IMPRINT",EDGE,{"disambiguationData":[TD([[makeQuery(id+"F0.imprint","INTERSECT",VERTEX,{"derivedFrom":[subQ0,sQuery(id+"F0.wireOp",EDGE,"E5.right")]}),-1.0]])],"derivedFrom":subQ0})])],"isStart":true});}
            var Q16;
            {var subQ0=sQuery(id+"F0.wireOp",EDGE,"E1.top");Q16=makeQuery(id+"F1.opExtrude","CAP_EDGE",EDGE,{"disambiguationData":[OSD([subQ0]),TDD([makeQuery(id+"F0.imprint","IMPRINT",EDGE,{"disambiguationData":[TD([[makeQuery(id+"F0.imprint","INTERSECT",VERTEX,{"derivedFrom":[subQ0,sQuery(id+"F0.wireOp",EDGE,"E9.left")]}),-1.0]])],"derivedFrom":subQ0})])],"isStart":true});}
            var Q17;
            {var subQ0=sQuery(id+"F0.wireOp",EDGE,"E1.top");Q17=makeQuery(id+"F1.opExtrude","CAP_EDGE",EDGE,{"disambiguationData":[OSD([subQ0]),TDD([makeQuery(id+"F0.imprint","IMPRINT",EDGE,{"disambiguationData":[TD([[makeQuery(id+"F0.imprint","INTERSECT",VERTEX,{"derivedFrom":[subQ0,sQuery(id+"F0.wireOp",EDGE,"E6.right")]}),-1.0]])],"derivedFrom":subQ0})])],"isStart":true});}
            var Q18;
            {var subQ0=sQuery(id+"F0.wireOp",EDGE,"E1.top");Q18=makeQuery(id+"F1.opExtrude","CAP_EDGE",EDGE,{"disambiguationData":[OSD([subQ0]),TDD([makeQuery(id+"F0.imprint","IMPRINT",EDGE,{"disambiguationData":[TD([[makeQuery(id+"F0.imprint","INTERSECT",VERTEX,{"derivedFrom":[subQ0,sQuery(id+"F0.wireOp",EDGE,"E7.right")]}),-1.0]])],"derivedFrom":subQ0})])],"isStart":true});}
            var Q19;
            {var subQ0=sQuery(id+"F0.wireOp",EDGE,"E8.trimOffspring");Q19=makeQuery(id+"F1.opExtrude","CAP_EDGE",EDGE,{"disambiguationData":[OSD([subQ0]),TDD([makeQuery(id+"F0.imprint","IMPRINT",EDGE,{"disambiguationData":[TD([[makeQuery(id+"F0.imprint","INTERSECT",VERTEX,{"derivedFrom":[sQuery(id+"F0.wireOp",EDGE,"E1.right"),subQ0]}),1.0]])],"derivedFrom":subQ0})])],"isStart":true});}
            var Q20;
            {var subQ0=sQuery(id+"F0.wireOp",EDGE,"E1.top");Q20=makeQuery(id+"F1.opExtrude","CAP_EDGE",EDGE,{"disambiguationData":[OSD([subQ0]),TDD([makeQuery(id+"F0.imprint","IMPRINT",EDGE,{"disambiguationData":[TD([[makeQuery(id+"F0.imprint","INTERSECT",VERTEX,{"derivedFrom":[subQ0,sQuery(id+"F0.wireOp",EDGE,"E3.left")]}),1.0]])],"derivedFrom":subQ0})])],"isStart":true});}
            var Q21;
            {var subQ0=sQuery(id+"F0.wireOp",EDGE,"E8.trimOffspring");Q21=makeQuery(id+"F1.opExtrude","CAP_EDGE",EDGE,{"disambiguationData":[OSD([subQ0]),TDD([makeQuery(id+"F0.imprint","IMPRINT",EDGE,{"disambiguationData":[TD([[makeQuery(id+"F0.imprint","INTERSECT",VERTEX,{"derivedFrom":[sQuery(id+"F0.wireOp",EDGE,"E6.bottom"),sQuery(id+"F0.wireOp",EDGE,"E6.right"),subQ0]}),-1.0]])],"derivedFrom":subQ0})])],"isStart":true});}
            var Q22;
            Q22=makeQuery(id+"F1.opExtrude","CAP_EDGE",EDGE,{"disambiguationData":[OSD([sQuery(id+"F0.wireOp",EDGE,"E23")])],"isStart":true});
            var Q23;
            Q23=makeQuery(id+"F1.opExtrude","CAP_EDGE",EDGE,{"disambiguationData":[OSD([sQuery(id+"F0.wireOp",EDGE,"E22")])],"isStart":true});
            var Q24;
            {var subQ0=sQuery(id+"F0.wireOp",EDGE,"E2.bottom");Q24=makeQuery(id+"F1.opExtrude","CAP_EDGE",EDGE,{"disambiguationData":[OSD([subQ0]),TDD([makeQuery(id+"F0.imprint","IMPRINT",EDGE,{"disambiguationData":[TD([[makeQuery(id+"F0.imprint","INTERSECT",VERTEX,{"derivedFrom":[subQ0,sQuery(id+"F0.wireOp",EDGE,"E4.right")]}),-1.0]])],"derivedFrom":subQ0})])],"isStart":true});}
            var Q25;
            {var subQ0=sQuery(id+"F0.wireOp",EDGE,"E2.bottom");Q25=makeQuery(id+"F1.opExtrude","CAP_EDGE",EDGE,{"disambiguationData":[OSD([subQ0]),TDD([makeQuery(id+"F0.imprint","IMPRINT",EDGE,{"disambiguationData":[TD([[makeQuery(id+"F0.imprint","INTERSECT",VERTEX,{"derivedFrom":[subQ0,sQuery(id+"F0.wireOp",EDGE,"E3.right")]}),-1.0]])],"derivedFrom":subQ0})])],"isStart":true});}
            var Q26;
            {var subQ0=sQuery(id+"F0.wireOp",EDGE,"E2.bottom");Q26=makeQuery(id+"F1.opExtrude","CAP_EDGE",EDGE,{"disambiguationData":[OSD([subQ0]),TDD([makeQuery(id+"F0.imprint","IMPRINT",EDGE,{"disambiguationData":[TD([[makeQuery(id+"F0.imprint","INTERSECT",VERTEX,{"derivedFrom":[sQuery(id+"F0.wireOp",EDGE,"E1.left"),subQ0]}),-1.0]])],"derivedFrom":subQ0})])],"isStart":true});}
            var Q27;
            {var subQ0=sQuery(id+"F0.wireOp",EDGE,"E1.left");Q27=makeQuery(id+"F1.opExtrude","CAP_EDGE",EDGE,{"disambiguationData":[OSD([subQ0]),TDD([makeQuery(id+"F0.imprint","IMPRINT",EDGE,{"disambiguationData":[TD([[makeQuery(id+"F0.imprint","INTERSECT",VERTEX,{"derivedFrom":[subQ0,sQuery(id+"F0.wireOp",EDGE,"E2.top")]}),1.0]])],"derivedFrom":subQ0})])],"isStart":true});}
            var Q28;
            Q28=makeQuery(id+"F1.opExtrude","CAP_EDGE",EDGE,{"disambiguationData":[OSD([sQuery(id+"F0.wireOp",EDGE,"E10.MirrorCS")])],"isStart":true});
            var Q29;
            Q29=makeQuery(id+"F1.opExtrude","CAP_EDGE",EDGE,{"disambiguationData":[OSD([sQuery(id+"F0.wireOp",EDGE,"E11.MirrorCS")])],"isStart":true});
            var Q30;
            Q30=makeQuery(id+"F1.opExtrude","CAP_EDGE",EDGE,{"disambiguationData":[OSD([sQuery(id+"F0.wireOp",EDGE,"E12.MirrorCS")])],"isStart":true});
            var Q31;
            Q31=makeQuery(id+"F1.opExtrude","CAP_EDGE",EDGE,{"disambiguationData":[OSD([sQuery(id+"F0.wireOp",EDGE,"E13.MirrorCS")])],"isStart":true});
            var Q32;
            Q32=makeQuery(id+"F1.opExtrude","CAP_EDGE",EDGE,{"disambiguationData":[OSD([sQuery(id+"F0.wireOp",EDGE,"E14.MirrorCS")])],"isStart":true});
            var Q33;
            Q33=makeQuery(id+"F1.opExtrude","CAP_EDGE",EDGE,{"disambiguationData":[OSD([sQuery(id+"F0.wireOp",EDGE,"E15.MirrorCS")])],"isStart":true});
            var Q34;
            Q34=makeQuery(id+"F1.opExtrude","CAP_EDGE",EDGE,{"disambiguationData":[OSD([sQuery(id+"F0.wireOp",EDGE,"E16.MirrorCS")])],"isStart":true});
            var Q35;
            Q35=makeQuery(id+"F1.opExtrude","CAP_EDGE",EDGE,{"disambiguationData":[OSD([sQuery(id+"F0.wireOp",EDGE,"E17.MirrorCS")])],"isStart":true});
            var Q36;
            Q36=makeQuery(id+"F1.opExtrude","CAP_EDGE",EDGE,{"disambiguationData":[OSD([sQuery(id+"F0.wireOp",EDGE,"E18.MirrorCS")])],"isStart":true});
            var Q37;
            Q37=makeQuery(id+"F1.opExtrude","CAP_EDGE",EDGE,{"disambiguationData":[OSD([sQuery(id+"F0.wireOp",EDGE,"E19.MirrorCS")])],"isStart":true});
            var Q38;
            Q38=makeQuery(id+"F1.opExtrude","CAP_EDGE",EDGE,{"disambiguationData":[OSD([sQuery(id+"F0.wireOp",EDGE,"E20.MirrorCS")])],"isStart":true});
            var Q39;
            Q39=makeQuery(id+"F1.opExtrude","CAP_EDGE",EDGE,{"disambiguationData":[OSD([sQuery(id+"F0.wireOp",EDGE,"E21.MirrorCS")])],"isStart":true});
            var Q40;
            {var subQ0=sQuery(id+"F0.wireOp",EDGE,"E1.right");Q40=makeQuery(id+"F1.opExtrude","CAP_EDGE",EDGE,{"disambiguationData":[OSD([subQ0]),TDD([makeQuery(id+"F0.imprint","IMPRINT",EDGE,{"disambiguationData":[TD([[makeQuery(id+"F0.imprint","INTERSECT",VERTEX,{"derivedFrom":[sQuery(id+"F0.wireOp",EDGE,"E1.bottom"),subQ0]}),-1.0]])],"derivedFrom":subQ0})])],"isStart":true});}
            var Q41;
            {var subQ0=sQuery(id+"F0.wireOp",EDGE,"E2.top");Q41=makeQuery(id+"F1.opExtrude","CAP_EDGE",EDGE,{"disambiguationData":[OSD([subQ0]),TDD([makeQuery(id+"F0.imprint","IMPRINT",EDGE,{"disambiguationData":[TD([[makeQuery(id+"F0.imprint","INTERSECT",VERTEX,{"derivedFrom":[subQ0,sQuery(id+"F0.wireOp",EDGE,"E21.MirrorCS")]}),-1.0]])],"derivedFrom":subQ0})])],"isStart":true});}
            var Q42;
            {var subQ0=sQuery(id+"F0.wireOp",EDGE,"E2.top");Q42=makeQuery(id+"F1.opExtrude","CAP_EDGE",EDGE,{"disambiguationData":[OSD([subQ0]),TDD([makeQuery(id+"F0.imprint","IMPRINT",EDGE,{"disambiguationData":[TD([[makeQuery(id+"F0.imprint","INTERSECT",VERTEX,{"derivedFrom":[subQ0,sQuery(id+"F0.wireOp",EDGE,"E19.MirrorCS")]}),-1.0]])],"derivedFrom":subQ0})])],"isStart":true});}
            var Q43;
            {var subQ0=sQuery(id+"F0.wireOp",EDGE,"E2.top");Q43=makeQuery(id+"F1.opExtrude","CAP_EDGE",EDGE,{"disambiguationData":[OSD([subQ0]),TDD([makeQuery(id+"F0.imprint","IMPRINT",EDGE,{"disambiguationData":[TD([[makeQuery(id+"F0.imprint","INTERSECT",VERTEX,{"derivedFrom":[subQ0,sQuery(id+"F0.wireOp",EDGE,"E17.MirrorCS")]}),-1.0]])],"derivedFrom":subQ0})])],"isStart":true});}
            var Q44;
            {var subQ0=sQuery(id+"F0.wireOp",EDGE,"E2.top");Q44=makeQuery(id+"F1.opExtrude","CAP_EDGE",EDGE,{"disambiguationData":[OSD([subQ0]),TDD([makeQuery(id+"F0.imprint","IMPRINT",EDGE,{"disambiguationData":[TD([[makeQuery(id+"F0.imprint","INTERSECT",VERTEX,{"derivedFrom":[subQ0,sQuery(id+"F0.wireOp",EDGE,"E15.MirrorCS")]}),-1.0]])],"derivedFrom":subQ0})])],"isStart":true});}
            var Q45;
            {var subQ0=sQuery(id+"F0.wireOp",EDGE,"E2.top");Q45=makeQuery(id+"F1.opExtrude","CAP_EDGE",EDGE,{"disambiguationData":[OSD([subQ0]),TDD([makeQuery(id+"F0.imprint","IMPRINT",EDGE,{"disambiguationData":[TD([[makeQuery(id+"F0.imprint","INTERSECT",VERTEX,{"derivedFrom":[subQ0,sQuery(id+"F0.wireOp",EDGE,"E13.MirrorCS")]}),-1.0]])],"derivedFrom":subQ0})])],"isStart":true});}
            var Q46;
            {var subQ0=sQuery(id+"F0.wireOp",EDGE,"E2.top");Q46=makeQuery(id+"F1.opExtrude","CAP_EDGE",EDGE,{"disambiguationData":[OSD([subQ0]),TDD([makeQuery(id+"F0.imprint","IMPRINT",EDGE,{"disambiguationData":[TD([[makeQuery(id+"F0.imprint","INTERSECT",VERTEX,{"derivedFrom":[subQ0,sQuery(id+"F0.wireOp",EDGE,"E11.MirrorCS")]}),-1.0]])],"derivedFrom":subQ0})])],"isStart":true});}
            var Q47;
            {var subQ0=sQuery(id+"F0.wireOp",EDGE,"E2.top");Q47=makeQuery(id+"F1.opExtrude","CAP_EDGE",EDGE,{"disambiguationData":[OSD([subQ0]),TDD([makeQuery(id+"F0.imprint","IMPRINT",EDGE,{"disambiguationData":[TD([[makeQuery(id+"F0.imprint","INTERSECT",VERTEX,{"derivedFrom":[sQuery(id+"F0.wireOp",EDGE,"E1.left"),subQ0]}),-1.0]])],"derivedFrom":subQ0})])],"isStart":true});}
            var Q48;
            {var subQ0=sQuery(id+"F0.wireOp",EDGE,"E1.bottom");Q48=makeQuery(id+"F1.opExtrude","CAP_EDGE",EDGE,{"disambiguationData":[OSD([subQ0]),TDD([makeQuery(id+"F0.imprint","IMPRINT",EDGE,{"disambiguationData":[TD([[makeQuery(id+"F0.imprint","INTERSECT",VERTEX,{"derivedFrom":[subQ0,sQuery(id+"F0.wireOp",EDGE,"E10.MirrorCS")]}),1.0]])],"derivedFrom":subQ0})])],"isStart":true});}
            var Q49;
            {var subQ0=sQuery(id+"F0.wireOp",EDGE,"E1.bottom");Q49=makeQuery(id+"F1.opExtrude","CAP_EDGE",EDGE,{"disambiguationData":[OSD([subQ0]),TDD([makeQuery(id+"F0.imprint","IMPRINT",EDGE,{"disambiguationData":[TD([[makeQuery(id+"F0.imprint","INTERSECT",VERTEX,{"derivedFrom":[subQ0,sQuery(id+"F0.wireOp",EDGE,"E11.MirrorCS")]}),-1.0]])],"derivedFrom":subQ0})])],"isStart":true});}
            var Q50;
            {var subQ0=sQuery(id+"F0.wireOp",EDGE,"E1.bottom");Q50=makeQuery(id+"F1.opExtrude","CAP_EDGE",EDGE,{"disambiguationData":[OSD([subQ0]),TDD([makeQuery(id+"F0.imprint","IMPRINT",EDGE,{"disambiguationData":[TD([[makeQuery(id+"F0.imprint","INTERSECT",VERTEX,{"derivedFrom":[subQ0,sQuery(id+"F0.wireOp",EDGE,"E13.MirrorCS")]}),-1.0]])],"derivedFrom":subQ0})])],"isStart":true});}
            var Q51;
            {var subQ0=sQuery(id+"F0.wireOp",EDGE,"E1.bottom");Q51=makeQuery(id+"F1.opExtrude","CAP_EDGE",EDGE,{"disambiguationData":[OSD([subQ0]),TDD([makeQuery(id+"F0.imprint","IMPRINT",EDGE,{"disambiguationData":[TD([[makeQuery(id+"F0.imprint","INTERSECT",VERTEX,{"derivedFrom":[subQ0,sQuery(id+"F0.wireOp",EDGE,"E15.MirrorCS")]}),-1.0]])],"derivedFrom":subQ0})])],"isStart":true});}
            var Q52;
            {var subQ0=sQuery(id+"F0.wireOp",EDGE,"E1.bottom");Q52=makeQuery(id+"F1.opExtrude","CAP_EDGE",EDGE,{"disambiguationData":[OSD([subQ0]),TDD([makeQuery(id+"F0.imprint","IMPRINT",EDGE,{"disambiguationData":[TD([[makeQuery(id+"F0.imprint","INTERSECT",VERTEX,{"derivedFrom":[subQ0,sQuery(id+"F0.wireOp",EDGE,"E17.MirrorCS")]}),-1.0]])],"derivedFrom":subQ0})])],"isStart":true});}
            var Q53;
            {var subQ0=sQuery(id+"F0.wireOp",EDGE,"E1.bottom");Q53=makeQuery(id+"F1.opExtrude","CAP_EDGE",EDGE,{"disambiguationData":[OSD([subQ0]),TDD([makeQuery(id+"F0.imprint","IMPRINT",EDGE,{"disambiguationData":[TD([[makeQuery(id+"F0.imprint","INTERSECT",VERTEX,{"derivedFrom":[subQ0,sQuery(id+"F0.wireOp",EDGE,"E19.MirrorCS")]}),-1.0]])],"derivedFrom":subQ0})])],"isStart":true});}
            var Q54;
            {var subQ0=sQuery(id+"F0.wireOp",EDGE,"E1.bottom");Q54=makeQuery(id+"F1.opExtrude","CAP_EDGE",EDGE,{"disambiguationData":[OSD([subQ0]),TDD([makeQuery(id+"F0.imprint","IMPRINT",EDGE,{"disambiguationData":[TD([[makeQuery(id+"F0.imprint","INTERSECT",VERTEX,{"derivedFrom":[subQ0,sQuery(id+"F0.wireOp",EDGE,"E1.right")]}),1.0]])],"derivedFrom":subQ0})])],"isStart":true});}
            var Q55;
            Q55=makeQuery(id+"F1.opExtrude","CAP_EDGE",EDGE,{"disambiguationData":[OSD([sQuery(id+"F0.wireOp",EDGE,"E0.right")])],"isStart":true});
            var Q56;
            Q56=makeQuery(id+"F1.opExtrude","CAP_EDGE",EDGE,{"disambiguationData":[OSD([sQuery(id+"F0.wireOp",EDGE,"E0.left")])],"isStart":true});
            var Q57;
            Q57=makeQuery(id+"F1.opExtrude","CAP_EDGE",EDGE,{"disambiguationData":[OSD([sQuery(id+"F0.wireOp",EDGE,"E0.bottom")])],"isStart":true});
            var Q58;
            Q58=makeQuery(id+"F1.opExtrude","CAP_EDGE",EDGE,{"disambiguationData":[OSD([sQuery(id+"F0.wireOp",EDGE,"E0.top")])],"isStart":true});
            fillet(context, id + "F3", {"entities" : qUnion([Q0, Q1, Q2, Q3, Q4, Q5, Q6, Q7, Q8, Q9, Q10, Q11, Q12, Q13, Q14, Q15, Q16, Q17, Q18, Q19, Q20, Q21, Q22, Q23, Q24, Q25, Q26, Q27, Q28, Q29, Q30, Q31, Q32, Q33, Q34, Q35, Q36, Q37, Q38, Q39, Q40, Q41, Q42, Q43, Q44, Q45, Q46, Q47, Q48, Q49, Q50, Q51, Q52, Q53, Q54, Q55, Q56, Q57, Q58]), "radius" : 1.27 * mm, "tangentPropagation" : true, "allowEdgeOverflow" : false});
        }
    });
